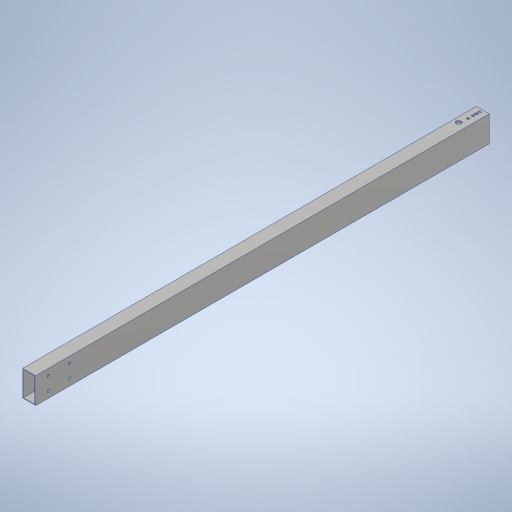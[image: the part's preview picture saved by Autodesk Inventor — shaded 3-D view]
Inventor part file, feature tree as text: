
AUTODESK INVENTOR PART (.ipt)
format: ipt  version: 2023.4 (Build 274418000, 418)  size: 311,808 bytes
history: native  units: in
note: dims shown in document units (in); Inventor stores cm internally (conversion verified against a paired STEP export)
features: sketch x4, hole x3, extrude x2, fillet x1, projected_geometry x1
ambient origin geometry x8: Origin, YZ Plane, XZ Plane, XY Plane, X Axis, Y Axis, Z Axis, Center Point
bodies: Solid1 (feature_tree)
feature tree (11):
  extrude  "Extrusion1"  Depth=0.5in
  hole  "Hole1"  [1 undecoded]
  hole  "Hole3"  [1 undecoded]
  extrude  "Extrusion2"  Depth=1.0in
  fillet  "Fillet1"  Radius=1.0in
  hole  "Hole4"  [1 undecoded]
  sketch  "Sketch2"  dims[d4=0.0in d5=0.5in]
  sketch  "Sketch4"  dims[d6=0.25in d7=0.25in]
  sketch  "Sketch5"  dims[d8=0.25in]
  sketch  "Sketch6"  dims[d9=0.201in d10=0.75in d11=0.385in d12=0.25in d13=0.5635in d14=1.0in d15=0.8108in d27=0.812in d28=0.391in d29=1.0in d30=0.375in d31=0.75in d32=0.385in d33=0.25in d34=0.5635in d35=1.0in d36=0.8108in d37=1.1in d38=1.25in d41=0.0625in d42=0.0in d43=1.75in d44=0.13in d45=0.375in d46=1.0in d47=0.5in d48=0.5in d49=1.625in d50=0.201in d51=0.75in d52=0.385in d53=0.25in d54=0.5635in d55=1.0in d56=0.8108in]
  projected_geometry  "Projected Loop1"
note: 3 required parameter values undecoded (feature->parameter linkage not recoverable at this tier; creation-order binding heuristic only, values carry confidence <= 0.55)
